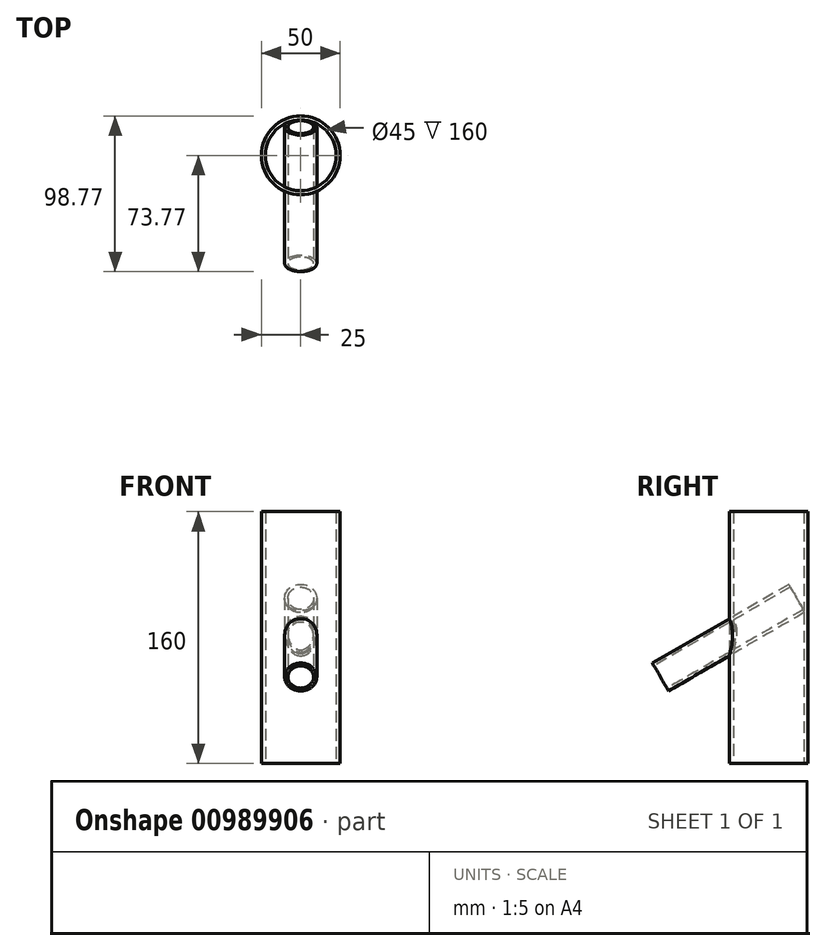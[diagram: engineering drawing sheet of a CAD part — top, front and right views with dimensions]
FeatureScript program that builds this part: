
annotation { "Feature Type Name" : "Feature", "Feature Type Description" : "" }
export const myFeature = defineFeature(function(context is Context, id is Id, definition is map)
    precondition{}
    {
        {
            var Q0;
            Q0=qCreatedBy(makeId("Top.planeOp"),FACE);
            var sketch = newSketch(context, id + "F0", { "sketchPlane" : qUnion([Q0])});
            skCircle(sketch, "E0", {"center": v(0, 0) * mm, "radius": 25 * mm});
            skCircle(sketch, "E1", {"center": v(0, 0) * mm, "radius": 22.5 * mm});
            skSolve(sketch);
        }
        {
            var Q0;
            Q0=makeQuery(id+"F0.imprint","IMPRINT",FACE,{"disambiguationData":[TD([[makeQuery(id+"F0.imprint","IMPRINT",EDGE,{"derivedFrom":sQuery(id+"F0.wireOp",EDGE,"E0")}),1.0]])]});
            extrude(context, id + "F1", {"entities" : qUnion([Q0]), "depth" : 160 * mm, "offsetDistance" : 25 * mm, "symmetric" : true});
        }
        {
            var Q0;
            Q0=qCreatedBy(makeId("Top.planeOp"),FACE);
            var sketch = newSketch(context, id + "F2", { "sketchPlane" : qUnion([Q0])});
            skLineSegment(sketch, "E2", {"start": v(-74.65, 0) * mm, "end": v(75.25, 0) * mm, "construction": true});
            skSolve(sketch);
        }
        {
            var Q0;
            Q0=sQuery(id+"F2.wireOp",EDGE,"E2");
            cPlane(context, id + "F3", {"entities" : qUnion([Q0]), "cplaneType" : CPlaneType.LINE_ANGLE, "offset" : 25 * mm, "angle" : 30 * degree, "width" : 150 * mm, "height" : 150 * mm});
        }
        {
            var Q0;
            Q0=qCreatedBy(id+"F3.planeOp",FACE);
            cPlane(context, id + "F4", {"entities" : qUnion([Q0]), "cplaneType" : CPlaneType.OFFSET, "offset" : 22 * mm, "oppositeDirection" : true, "width" : 150 * mm, "height" : 150 * mm});
        }
        {
            var Q0;
            Q0=qCreatedBy(id+"F4.planeOp",FACE);
            var sketch = newSketch(context, id + "F5", { "sketchPlane" : qUnion([Q0])});
            skCircle(sketch, "E3", {"center": v(0, 12.64) * mm, "radius": 10.2 * mm});
            skCircle(sketch, "E4.0", {"center": v(0, 12.64) * mm, "radius": 8.2 * mm});
            skSolve(sketch);
        }
        {
            var Q0;
            Q0 = qSketchRegion(id + "F5", true);
            extrude(context, id + "F6", {"entities" : qUnion([Q0]), "operationType" : NewBodyOperationType.ADD, "depth" : 100 * mm, "offsetDistance" : 25 * mm, "symmetric" : true});
        }
    });
